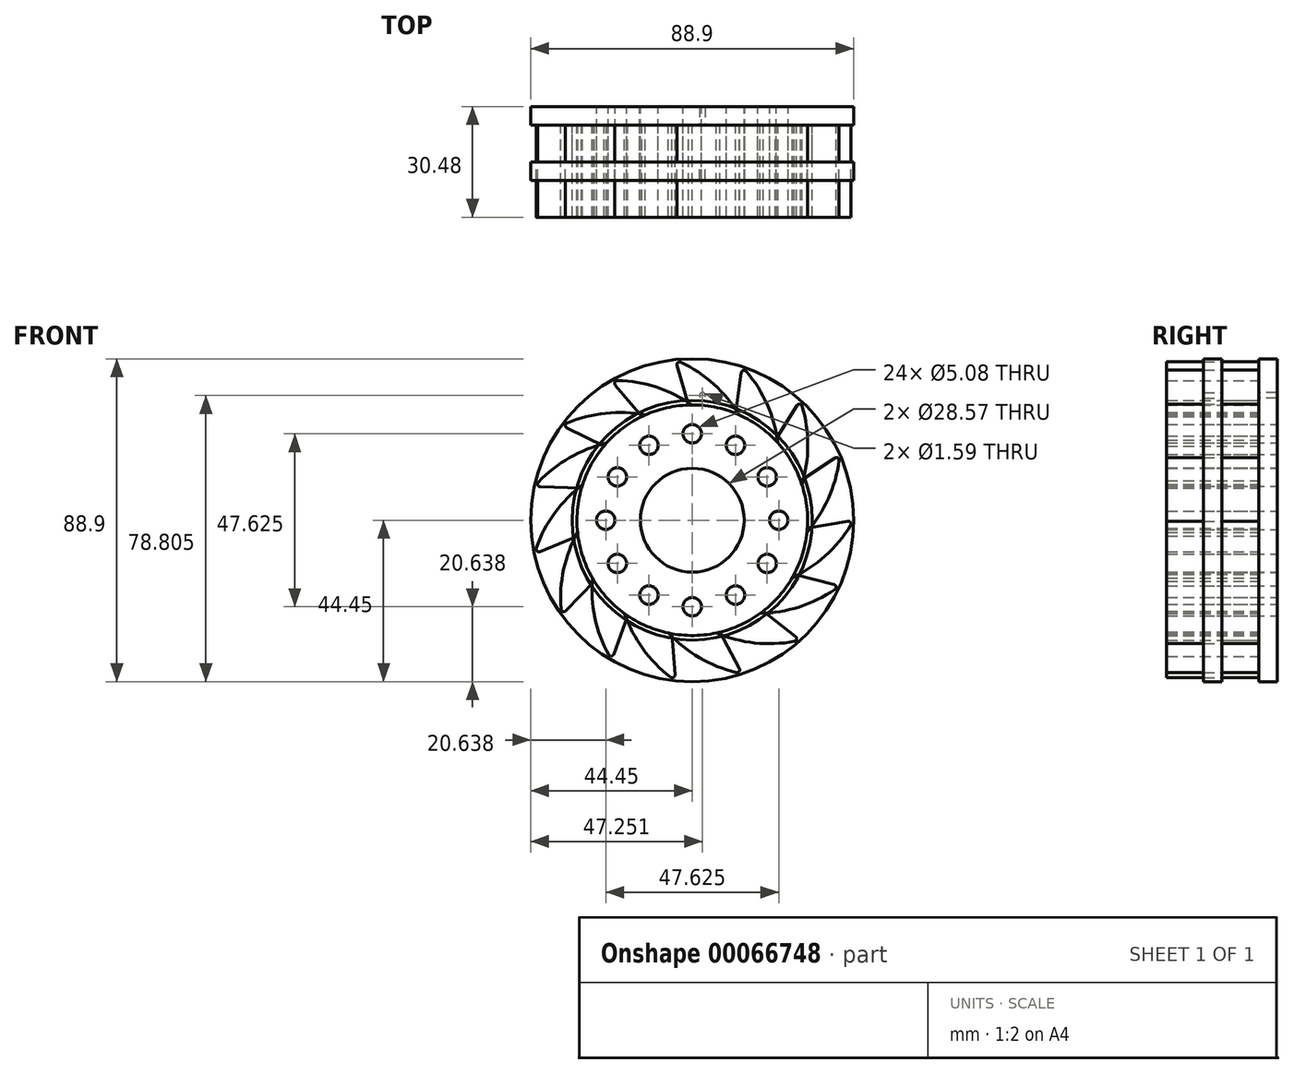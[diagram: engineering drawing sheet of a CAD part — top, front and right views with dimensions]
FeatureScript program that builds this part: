
annotation { "Feature Type Name" : "Feature", "Feature Type Description" : "" }
export const myFeature = defineFeature(function(context is Context, id is Id, definition is map)
    precondition{}
    {
        {
            var Q0;
            Q0=qCreatedBy(makeId("Front.planeOp"),FACE);
            var sketch = newSketch(context, id + "F0", { "sketchPlane" : qUnion([Q0])});
            skCircle(sketch, "E0", {"center": v(0, 0) * mm, "radius": 14.29 * mm});
            skCircle(sketch, "E1", {"center": v(0, 0) * mm, "radius": 33.02 * mm});
            skCircle(sketch, "E2", {"center": v(0, 0) * mm, "radius": 44.45 * mm});
            skCircle(sketch, "E3", {"center": v(-20.62, 11.9) * mm, "radius": 2.54 * mm});
            skCircle(sketch, "E4.1.0", {"center": v(-11.9, 20.62) * mm, "radius": 2.54 * mm});
            skCircle(sketch, "E4.2.0", {"center": v(0, 23.81) * mm, "radius": 2.54 * mm});
            skLineSegment(sketch, "E4.anchor1", {"start": v(0, 0) * mm, "end": v(-20.62, 11.9) * mm, "construction": true});
            skLineSegment(sketch, "E4.anchor2", {"start": v(0, 0) * mm, "end": v(-23.81, 0) * mm, "construction": true});
            skCircle(sketch, "E5.1.3.0", {"center": v(11.9, 20.62) * mm, "radius": 2.54 * mm});
            skCircle(sketch, "E5.1.4.0", {"center": v(20.62, 11.9) * mm, "radius": 2.54 * mm});
            skCircle(sketch, "E5.1.5.0", {"center": v(23.81, 0) * mm, "radius": 2.54 * mm});
            skCircle(sketch, "E5.1.6.0", {"center": v(20.62, -11.9) * mm, "radius": 2.54 * mm});
            skCircle(sketch, "E5.1.7.0", {"center": v(11.9, -20.62) * mm, "radius": 2.54 * mm});
            skCircle(sketch, "E5.1.8.0", {"center": v(0, -23.81) * mm, "radius": 2.54 * mm});
            skCircle(sketch, "E5.1.9.0", {"center": v(-11.9, -20.62) * mm, "radius": 2.54 * mm});
            skCircle(sketch, "E5.1.10.0", {"center": v(-20.62, -11.9) * mm, "radius": 2.54 * mm});
            skCircle(sketch, "E5.1.11.0", {"center": v(-23.81, 0) * mm, "radius": 2.54 * mm});
            skCircle(sketch, "E6", {"center": v(2.8, 34.36) * mm, "radius": 0.8 * mm});
            skCircle(sketch, "E7", {"center": v(0, 0) * mm, "radius": 23.81 * mm, "construction": true});
            skSolve(sketch);
        }
        {
            var Q0;
            Q0=makeQuery(id+"F0.imprint","IMPRINT",FACE,{"disambiguationData":[TD([[makeQuery(id+"F0.imprint","IMPRINT",EDGE,{"derivedFrom":sQuery(id+"F0.wireOp",EDGE,"E1")}),1.0]])]});
            var Q1;
            Q1=makeQuery(id+"F0.imprint","IMPRINT",FACE,{"disambiguationData":[TD([[makeQuery(id+"F0.imprint","IMPRINT",EDGE,{"derivedFrom":sQuery(id+"F0.wireOp",EDGE,"E0")}),-1.0]])]});
            extrude(context, id + "F1", {"entities" : qUnion([Q0, Q1]), "depth" : 5.08 * mm});
        }
        {
            var Q0;
            Q0 = qSketchRegion(id + "F0", true);
            var Q1;
            Q1=makeQuery(id+"F0.imprint","IMPRINT",FACE,{"disambiguationData":[TD([[makeQuery(id+"F0.imprint","IMPRINT",EDGE,{"derivedFrom":sQuery(id+"F0.wireOp",EDGE,"E0")}),-1.0]])]});
            extrude(context, id + "F2", {"entities" : qUnion([Q0, Q1]), "operationType" : NewBodyOperationType.ADD, "oppositeDirection" : true, "depth" : 5.08 * mm});
        }
        {
            var Q0;
            Q0=makeQuery(id+"F1.opExtrude","SWEPT_BODY",BODY,{"disambiguationData":[OSD([sQuery(id+"F0.wireOp",EDGE,"E0"),sQuery(id+"F0.wireOp",EDGE,"E1"),sQuery(id+"F0.wireOp",EDGE,"E3"),sQuery(id+"F0.wireOp",EDGE,"E4.1.0"),sQuery(id+"F0.wireOp",EDGE,"E4.2.0"),sQuery(id+"F0.wireOp",EDGE,"E5.1.3.0"),sQuery(id+"F0.wireOp",EDGE,"E5.1.4.0"),sQuery(id+"F0.wireOp",EDGE,"E5.1.5.0"),sQuery(id+"F0.wireOp",EDGE,"E5.1.6.0"),sQuery(id+"F0.wireOp",EDGE,"E5.1.7.0"),sQuery(id+"F0.wireOp",EDGE,"E5.1.8.0"),sQuery(id+"F0.wireOp",EDGE,"E5.1.9.0"),sQuery(id+"F0.wireOp",EDGE,"E5.1.10.0"),sQuery(id+"F0.wireOp",EDGE,"E5.1.11.0")])]});
            var Q1;
            Q1=makeQuery(id+"F1.opExtrude","CAP_FACE",FACE,{"disambiguationData":[OSD([sQuery(id+"F0.wireOp",EDGE,"E0"),sQuery(id+"F0.wireOp",EDGE,"E1"),sQuery(id+"F0.wireOp",EDGE,"E3"),sQuery(id+"F0.wireOp",EDGE,"E4.1.0"),sQuery(id+"F0.wireOp",EDGE,"E4.2.0"),sQuery(id+"F0.wireOp",EDGE,"E5.1.3.0"),sQuery(id+"F0.wireOp",EDGE,"E5.1.4.0"),sQuery(id+"F0.wireOp",EDGE,"E5.1.5.0"),sQuery(id+"F0.wireOp",EDGE,"E5.1.6.0"),sQuery(id+"F0.wireOp",EDGE,"E5.1.7.0"),sQuery(id+"F0.wireOp",EDGE,"E5.1.8.0"),sQuery(id+"F0.wireOp",EDGE,"E5.1.9.0"),sQuery(id+"F0.wireOp",EDGE,"E5.1.10.0"),sQuery(id+"F0.wireOp",EDGE,"E5.1.11.0")])],"isStart":false});
            mirror(context, id + "F3", {"operationType" : NewBodyOperationType.ADD, "entities" : qUnion([Q0]), "mirrorPlane" : qUnion([Q1])});
        }
        {
            var Q0;
            Q0=makeQuery(id+"F0.imprint","IMPRINT",FACE,{"disambiguationData":[TD([[makeQuery(id+"F0.imprint","IMPRINT",EDGE,{"derivedFrom":sQuery(id+"F0.wireOp",EDGE,"E0")}),-1.0]])]});
            extrude(context, id + "F4", {"entities" : qUnion([Q0]), "depth" : 25.4 * mm});
        }
        {
            var Q0;
            Q0=qCreatedBy(makeId("Front.planeOp"),FACE);
            var sketch = newSketch(context, id + "F5", { "sketchPlane" : qUnion([Q0])});
            skArc(sketch, "E8", {"start": v(0, 31.75) * mm, "mid": v(-9.8, 36.6) * mm, "end": v(-20.56, 38.48) * mm});
            skLineSegment(sketch, "E9", {"start": v(0, 31.75) * mm, "end": v(0, 12) * mm});
            skLineSegment(sketch, "E10", {"start": v(0, 12) * mm, "end": v(-21.17, 37.23) * mm});
            skLineSegment(sketch, "E11", {"start": v(0, 0) * mm, "end": v(-22.23, 38.5) * mm, "construction": true});
            skCircle(sketch, "E12.0", {"center": v(0, 0) * mm, "radius": 31.75 * mm});
            skPoint(sketch, "E13.visualSharp", {"position": v(-22.23, 38.5) * mm});
            skArc(sketch, "E13.filletArc", {"start": v(-20.56, 38.48) * mm, "mid": v(-21.27, 38.05) * mm, "end": v(-21.17, 37.23) * mm});
            skSolve(sketch);
        }
        {
            var Q0;
            {var subQ0=sQuery(id+"F5.wireOp",EDGE,"E8");Q0=makeQuery(id+"F5.imprint","IMPRINT",FACE,{"disambiguationData":[TD([[makeQuery(id+"F5.imprint","IMPRINT",EDGE,{"derivedFrom":subQ0}),1.0]])]});}
            extrude(context, id + "F6", {"entities" : qUnion([Q0]), "depth" : 25.4 * mm});
        }
        {
            var Q0;
            Q0=makeQuery(id+"F6.opExtrude","SWEPT_BODY",BODY,{"disambiguationData":[OSD([sQuery(id+"F5.wireOp",EDGE,"E8"),sQuery(id+"F5.wireOp",EDGE,"E9"),sQuery(id+"F5.wireOp",EDGE,"E10"),sQuery(id+"F5.wireOp",EDGE,"E12.0")])]});
            var Q1;
            Q1=sQuery(id+"F0.wireOp",EDGE,"E0");
            circularPattern(context, id + "F7", {"entities" : qUnion([Q0]), "axis" : qUnion([Q1]), "angle" : 360 * degree, "instanceCount" : 15, "equalSpace" : true});
        }
    });
